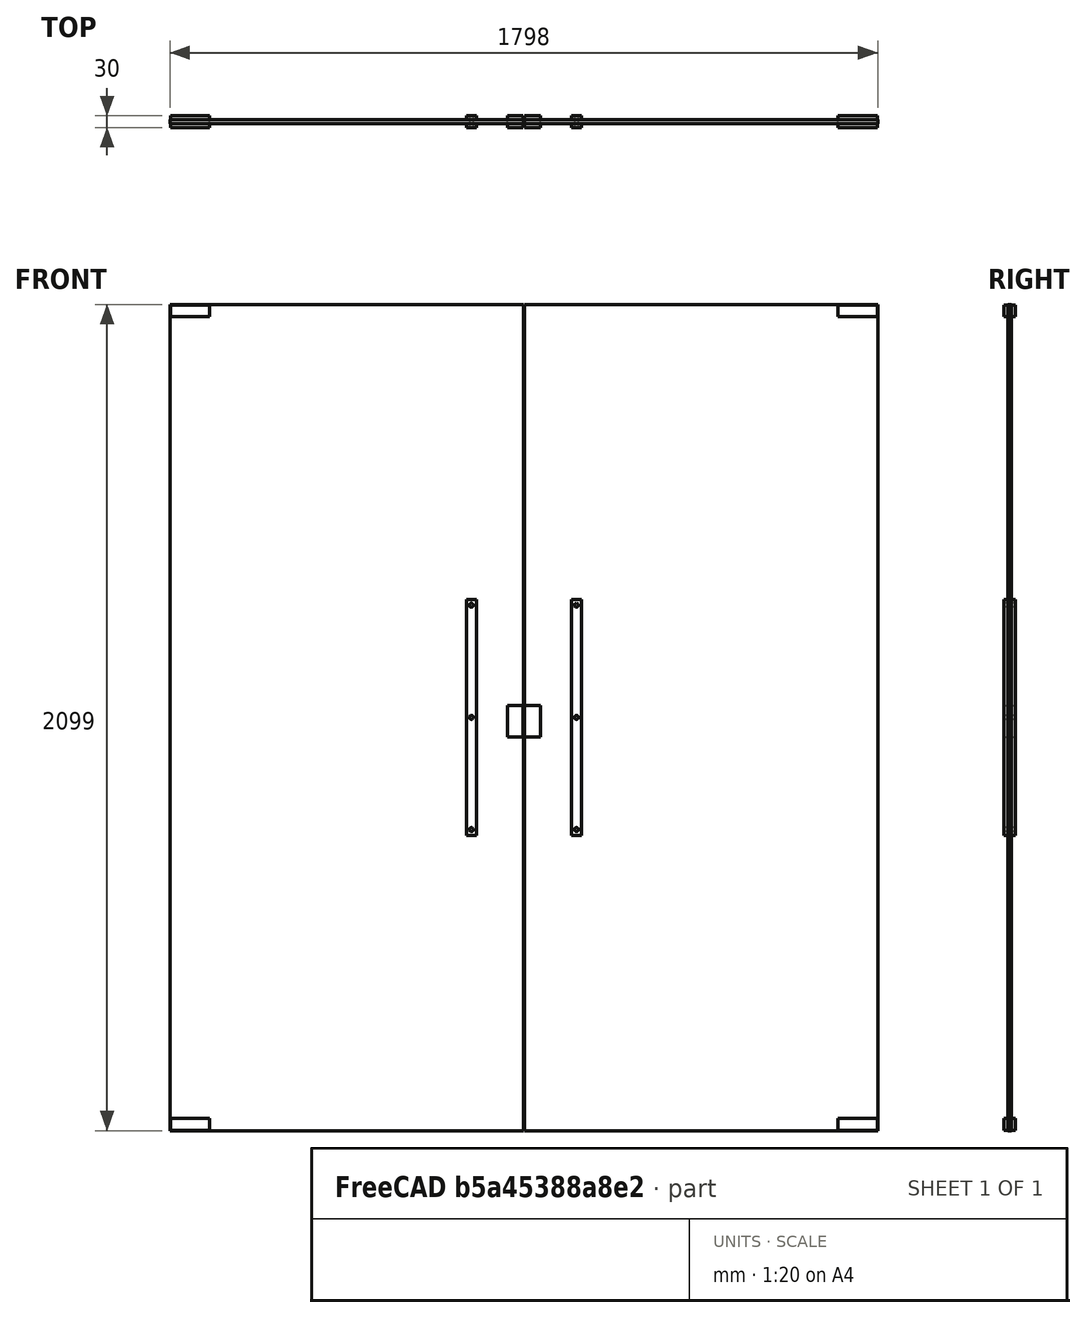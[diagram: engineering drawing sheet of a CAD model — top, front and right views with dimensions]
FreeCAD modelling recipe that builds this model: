
FCSTD DOCUMENT  (FreeCAD 0.16R6704 (Git))
Label: Double glass doors with handles
License: CreativeCommons Attribution
LicenseURL: http://creativecommons.org/licenses/by/4.0/
objects: Sketcher::SketchObject×3, Part::FeaturePython×1, App::DocumentObjectGroup×1
note: 4 computed .brp shape members not serialized (recipe doc carries the construction recipe); baked Part::Feature solids carry a one-line shape summary decoded from their .brp

FEATURE [Sketcher::SketchObject] Sketch124
  Placement = pos=(0,0,0) rot=(1,0,0;1.5708rad)
  sketch-geometry (59):
    g0: LineSegment StartX=0 StartY=0 StartZ=0 EndX=1800 EndY=0 EndZ=0
    g1: LineSegment StartX=1800 StartY=0 StartZ=0 EndX=1800 EndY=2100 EndZ=0
    g2: LineSegment StartX=1800 StartY=2100 StartZ=0 EndX=0 EndY=2100 EndZ=0
    g3: LineSegment StartX=0 StartY=2100 StartZ=0 EndX=0 EndY=0 EndZ=0
    g4: LineSegment StartX=1 StartY=0 StartZ=0 EndX=899 EndY=0 EndZ=0
    g5: LineSegment StartX=899 StartY=0 StartZ=0 EndX=899 EndY=2099 EndZ=0
    g6: LineSegment StartX=899 StartY=2099 StartZ=0 EndX=1 EndY=2099 EndZ=0
    g7: LineSegment StartX=1 StartY=2099 StartZ=0 EndX=1 EndY=0 EndZ=0
    g8: LineSegment StartX=2 StartY=2098 StartZ=0 EndX=102 EndY=2098 EndZ=0
    g9: LineSegment StartX=102 StartY=2098 StartZ=0 EndX=102 EndY=2068 EndZ=0
    g10: LineSegment StartX=102 StartY=2068 StartZ=0 EndX=2 EndY=2068 EndZ=0
    g11: LineSegment StartX=2 StartY=2068 StartZ=0 EndX=2 EndY=2098 EndZ=0
    g12: LineSegment StartX=2 StartY=1 StartZ=0 EndX=102 EndY=1 EndZ=0
    g13: LineSegment StartX=102 StartY=1 StartZ=0 EndX=102 EndY=31 EndZ=0
    g14: LineSegment StartX=102 StartY=31 StartZ=0 EndX=2 EndY=31 EndZ=0
    g15: LineSegment StartX=2 StartY=31 StartZ=0 EndX=2 EndY=1 EndZ=0
    g16: LineSegment StartX=858 StartY=1080 StartZ=0 EndX=898 EndY=1080 EndZ=0
    g17: LineSegment StartX=898 StartY=1080 StartZ=0 EndX=898 EndY=1000 EndZ=0
    g18: LineSegment StartX=898 StartY=1000 StartZ=0 EndX=858 EndY=1000 EndZ=0
    g19: LineSegment StartX=858 StartY=1000 StartZ=0 EndX=858 EndY=1080 EndZ=0
    g20: LineSegment StartX=754 StartY=1350 StartZ=0 EndX=779 EndY=1350 EndZ=0
    g21: LineSegment StartX=779 StartY=1350 StartZ=0 EndX=779 EndY=750 EndZ=0
    g22: LineSegment StartX=779 StartY=750 StartZ=0 EndX=754 EndY=750 EndZ=0
    g23: LineSegment StartX=754 StartY=750 StartZ=0 EndX=754 EndY=1350 EndZ=0
    g24: LineSegment [constr] StartX=766.5 StartY=1477.64 StartZ=0 EndX=766.5 EndY=711 EndZ=0
    g25: Circle CenterX=766.5 CenterY=1335 CenterZ=0 NormalX=0 NormalY=0 NormalZ=1 Radius=5
    g26: Circle CenterX=766.5 CenterY=1050 CenterZ=0 NormalX=0 NormalY=0 NormalZ=1 Radius=5
    g27: Circle CenterX=766.5 CenterY=765 CenterZ=0 NormalX=0 NormalY=0 NormalZ=1 Radius=5
    g28: LineSegment [constr] StartX=712 StartY=1050 StartZ=0 EndX=790 EndY=1050 EndZ=0
    g29: LineSegment [constr] StartX=900 StartY=2725.39 StartZ=0 EndX=900 EndY=-391.222 EndZ=0
    g30: LineSegment StartX=1799 StartY=1e-12 StartZ=0 EndX=901 EndY=1e-12 EndZ=0
    g31: LineSegment StartX=901 StartY=1e-12 StartZ=0 EndX=901 EndY=2099 EndZ=0
    g32: LineSegment StartX=901 StartY=2099 StartZ=0 EndX=1799 EndY=2099 EndZ=0
    g33: LineSegment StartX=1799 StartY=2099 StartZ=0 EndX=1799 EndY=1e-12 EndZ=0
    g34: LineSegment StartX=1798 StartY=2098 StartZ=0 EndX=1698 EndY=2098 EndZ=0
    g35: LineSegment StartX=1698 StartY=2098 StartZ=0 EndX=1698 EndY=2068 EndZ=0
    g36: LineSegment StartX=1698 StartY=2068 StartZ=0 EndX=1798 EndY=2068 EndZ=0
    g37: LineSegment StartX=1798 StartY=2068 StartZ=0 EndX=1798 EndY=2098 EndZ=0
    g38: LineSegment StartX=1798 StartY=1 StartZ=0 EndX=1698 EndY=1 EndZ=0
    g39: LineSegment StartX=1698 StartY=1 StartZ=0 EndX=1698 EndY=31 EndZ=0
    g40: LineSegment StartX=1698 StartY=31 StartZ=0 EndX=1798 EndY=31 EndZ=0
    g41: LineSegment StartX=1798 StartY=31 StartZ=0 EndX=1798 EndY=1 EndZ=0
    g42: LineSegment StartX=942 StartY=1080 StartZ=0 EndX=902 EndY=1080 EndZ=0
    g43: LineSegment StartX=902 StartY=1080 StartZ=0 EndX=902 EndY=1000 EndZ=0
    g44: LineSegment StartX=902 StartY=1000 StartZ=0 EndX=942 EndY=1000 EndZ=0
    g45: LineSegment StartX=942 StartY=1000 StartZ=0 EndX=942 EndY=1080 EndZ=0
    g46: LineSegment StartX=1046 StartY=1350 StartZ=0 EndX=1021 EndY=1350 EndZ=0
    g47: LineSegment StartX=1021 StartY=1350 StartZ=0 EndX=1021 EndY=750 EndZ=0
    g48: LineSegment StartX=1021 StartY=750 StartZ=0 EndX=1046 EndY=750 EndZ=0
    g49: LineSegment StartX=1046 StartY=750 StartZ=0 EndX=1046 EndY=1350 EndZ=0
    g50: LineSegment [constr] StartX=1033.5 StartY=1477.64 StartZ=0 EndX=1033.5 EndY=711 EndZ=0
    g51: Circle CenterX=1033.5 CenterY=1335 CenterZ=0 NormalX=0 NormalY=0 NormalZ=1 Radius=5
    g52: Circle CenterX=1033.5 CenterY=1050 CenterZ=0 NormalX=0 NormalY=0 NormalZ=1 Radius=5
    g53: Circle CenterX=1033.5 CenterY=765 CenterZ=0 NormalX=0 NormalY=0 NormalZ=1 Radius=5
    g54: LineSegment [constr] StartX=1088 StartY=1050 StartZ=0 EndX=1010 EndY=1050 EndZ=0
    g55: LineSegment StartX=-1 StartY=2101 StartZ=0 EndX=1801 EndY=2101 EndZ=0
    g56: LineSegment StartX=1801 StartY=2101 StartZ=0 EndX=1801 EndY=0 EndZ=0
    g57: LineSegment StartX=1801 StartY=0 StartZ=0 EndX=-1 EndY=0 EndZ=0
    g58: LineSegment StartX=-1 StartY=0 StartZ=0 EndX=-1 EndY=2101 EndZ=0
  constraints (150):
    c: Coincident(g0,g1)
    c: Coincident(g1,g2)
    c: Coincident(g2,g3)
    c: Coincident(g3,g0)
    c: Horizontal(g0)
    c: Horizontal(g2)
    c: Vertical(g1)
    c: Vertical(g3)
    c: Coincident(g4,g5)
    c: Coincident(g5,g6)
    c: Coincident(g6,g7)
    c: Coincident(g7,g4)
    c: Horizontal(g4)
    c: Horizontal(g6)
    c: Vertical(g5)
    c: Vertical(g7)
    c: DistanceY(g1) = 2100  'Altura vão'
    c: DistanceX(g0) = 1800  'Largura vão'
    c: DistanceY(g6,g2) = 1
    c: DistanceX(g2,g6) = 1
    c: DistanceY(g0,g4) = 0
    c: Coincident(g0,g-1)
    c: Coincident(g8,g9)
    c: Coincident(g9,g10)
    c: Coincident(g10,g11)
    c: Coincident(g11,g8)
    c: Horizontal(g8)
    c: Horizontal(g10)
    c: Vertical(g9)
    c: Vertical(g11)
    c: Coincident(g12,g13)
    c: Coincident(g13,g14)
    c: Coincident(g14,g15)
    c: Coincident(g15,g12)
    c: Horizontal(g12)
    c: Horizontal(g14)
    c: Vertical(g13)
    c: Vertical(g15)
    c: Coincident(g16,g17)
    c: Coincident(g17,g18)
    c: Coincident(g18,g19)
    c: Coincident(g19,g16)
    c: Horizontal(g16)
    c: Horizontal(g18)
    c: Vertical(g17)
    c: Vertical(g19)
    c: DistanceY(g8,g6) = 1
    c: DistanceX(g6,g8) = 1
    c: DistanceY(g9,g8) = 30  'Altura apoio'
    c: DistanceX(g10,g9) = 100  'Largura apoio'
    c: Equal(g9,g13)
    c: Equal(g14,g8)
    c: DistanceX(g4,g12) = 1
    c: DistanceY(g4,g12) = 1
    c: DistanceX(g17,g4) = 1
    c: DistanceY(g18,g16) = 80  'Altura da tranca'
    c: DistanceX(g16,g16) = 40  'Largura da tranca'
    c: DistanceY(g4,g18) = 1000  'Altura da tranca ao chão'
    c: Coincident(g20,g21)
    c: Coincident(g21,g22)
    c: Coincident(g22,g23)
    c: Coincident(g23,g20)
    c: Horizontal(g20)
    c: Horizontal(g22)
    c: Vertical(g21)
    c: Vertical(g23)
    c: DistanceX(g20,g20) = 25  'Largura puxador'
    c: DistanceY(g21,g20) = 600  'altura do puxador'
    c: Vertical(g24)  'Constraint69'
    c: Symmetric(g20,g20,g24)
    c: PointOnObject(g25,g24)  'Constraint72'
    c: PointOnObject(g26,g24)
    c: PointOnObject(g27,g24)
    c: Radius(g27) = 5  'Apoio puxador'
    c: Equal(g27,g26)  'Constraint83'
    c: Equal(g27,g25)  'Constraint82'
    c: DistanceY(g25,g20) = 15
    c: DistanceY(g21,g27) = 15
    c: Horizontal(g28)
    c: PointOnObject(g26,g28)
    c: Symmetric(g22,g20,g28)
    c: DistanceY(g4,g21) = 750  'Distância do puxador ao solo'
    c: DistanceX(g21,g4) = 120  'Distância do puxador'
    c: Vertical(g29)
    c: Symmetric(g2,g1,g29)
    c: Coincident(g30,g31)
    c: Coincident(g31,g32)
    c: Coincident(g32,g33)
    c: Coincident(g33,g30)
    c: Horizontal(g30)
    c: Horizontal(g32)
    c: Vertical(g31)
    c: Vertical(g33)
    c: Coincident(g34,g35)
    c: Coincident(g35,g36)
    c: Coincident(g36,g37)
    c: Coincident(g37,g34)
    c: Horizontal(g34)
    c: Horizontal(g36)
    c: Vertical(g35)
    c: Vertical(g37)
    c: Coincident(g38,g39)
    c: Coincident(g39,g40)
    c: Coincident(g40,g41)
    c: Coincident(g41,g38)
    c: Horizontal(g38)
    c: Horizontal(g40)
    c: Vertical(g39)
    c: Vertical(g41)
    c: Coincident(g42,g43)
    c: Coincident(g43,g44)
    c: Coincident(g44,g45)
    c: Coincident(g45,g42)
    c: Horizontal(g42)
    c: Horizontal(g44)
    c: Vertical(g43)
    c: Vertical(g45)
    c: Equal(g35,g39)
    c: Equal(g40,g34)
    c: Coincident(g46,g47)
    c: Coincident(g47,g48)
    c: Coincident(g48,g49)
    c: Coincident(g49,g46)
    c: Horizontal(g46)
    c: Horizontal(g48)
    c: Vertical(g47)
    c: Vertical(g49)
    c: Vertical(g50)  'Constraint69'
    c: Symmetric(g46,g46,g50)
    c: PointOnObject(g51,g50)  'Constraint72'
    c: PointOnObject(g52,g50)
    c: PointOnObject(g53,g50)
    c: Radius(g53) = 5  'Apoio puxador'
    c: Equal(g53,g52)  'Constraint83'
    c: Equal(g53,g51)  'Constraint82'
    c: Horizontal(g54)
    c: PointOnObject(g52,g54)
    c: Symmetric(g48,g46,g54)
    c: Coincident(g55,g56)
    c: Coincident(g56,g57)
    c: Coincident(g57,g58)
    c: Coincident(g58,g55)
    c: Horizontal(g55)
    c: Horizontal(g57)
    c: Vertical(g56)
    c: Vertical(g58)
    c: DistanceX(g55,g2) = 1
    c: DistanceY(g2,g55) = 1
    c: DistanceX(g1,g55) = 1
    c: DistanceY(g57,g-1) = 0
FEATURE [Part::FeaturePython] Window091  label="Double glass doors with handles 001"  # WARN: FeaturePython — macro-defined, semantics opaque (R4)
  Base = -> Sketch124
  Height = 2100
  HoleDepth = 0
  MoveWithHost = true
  Normal = (0,1,0)
  Preset = 6
  Role = 1
  Width = 900
  WindowParts = PORTA 1 | Glass panel | Wire1 | 10.0 | 10.0 | APOIO SUPERIOR PORTA 1 | Frame | Wire2 | 30.0 | 0.0 | APOIO INFERIOR PORTA 1 | Frame | Wire3 | 30.0 | 0.0 | TRANCA 1 | Frame | Wire4 | 30.0 | 0.0 | PUXADOR 1a | Frame | Wire5 | 10.0 | 0.0 | PUXADOR 2 | Frame | Wire13 | 10.0 | 0.0 | APOIO SUPERIRO PUXADOR 1 | Frame | Wire6 | 30.0 | 0.0 | APOIO CENTRAL PUXADOR 1 | Frame | Wire7 | 30.0 | 0.0 | APOIO INFERIRO PUXADOR 1 | Frame | Wire8 | 30.0 | 0.0 | PORTA 2 | Glass panel | Wire9 | 10.0 | 10.0 | APOIOS SUPERIRO PORTA 2 | Frame | Wire10 | 30.0 | 0.0 | APOIO INFERIRO PORTA 2 | Frame | Wire11 | 30.0 | 0.0 | TRANCA 2 | Frame | Wire12 | 30.0 | 0.0 | APOIO SUPERIOR PUXADOR 2 | Frame | Wire14 | 30.0 | 0.0 | APOIO CENTRAL PUXADOR 2 | Frame | Wire15 | 30.0 | 0.0 | APOIO INFERIOR PUXADOR 2 | Frame | Wire16 | 30.0 | 0.0 | PUXADOR 2b | Frame | Wire13 | 10.0 | 20.0 | PUXADOR 1B | Frame | Wire5 | 10.0 | 20.0
FEATURE [Sketcher::SketchObject] Sketch126  label="Opening indication"
  ExternalGeometry = -> [Window091]
  Placement = pos=(0,10,0) rot=(1,0,0;1.5708rad)
  Support = -> Window091 [Face5]
  sketch-geometry (6):
    g0: LineSegment [constr] StartX=-578.323 StartY=1041.81 StartZ=0 EndX=1784.68 EndY=1041.81 EndZ=0
    g1: LineSegment [constr] StartX=60 StartY=2218.7 StartZ=0 EndX=60 EndY=-135.607 EndZ=0
    g2: LineSegment StartX=1 StartY=1041.81 StartZ=0 EndX=60 EndY=2099 EndZ=0
    g3: LineSegment StartX=60 StartY=2099 StartZ=0 EndX=899 EndY=1041.81 EndZ=0
    g4: LineSegment StartX=899 StartY=1041.81 StartZ=0 EndX=60 EndY=0 EndZ=0
    g5: LineSegment StartX=60 StartY=0 StartZ=0 EndX=1 EndY=1041.81 EndZ=0
  constraints (16):
    c: Horizontal(g0)
    c: DistanceY(g-1,g0) = 1041.81  'Altura tranca'
    c: Vertical(g1)
    c: PointOnObject(g2,g-4)
    c: PointOnObject(g2,g-3)
    c: Coincident(g2,g3)
    c: PointOnObject(g3,g-5)
    c: Coincident(g3,g4)
    c: PointOnObject(g4,g-6)
    c: Coincident(g4,g5)
    c: Coincident(g5,g2)
    c: PointOnObject(g2,g0)
    c: PointOnObject(g2,g1)
    c: PointOnObject(g3,g0)
    c: PointOnObject(g4,g1)
    c: DistanceX(g-1,g1) = 60  'Eixo porta'
FEATURE [Sketcher::SketchObject] Sketch127  label="Opening indication  "
  ExternalGeometry = -> [Window091]
  Placement = pos=(0,10,0) rot=(1,0,0;1.5708rad)
  Support = -> Window091 [Face50]
  sketch-geometry (6):
    g0: LineSegment [constr] StartX=-496.649 StartY=1041.19 StartZ=0 EndX=2033.7 EndY=1041.19 EndZ=0
    g1: LineSegment StartX=1739 StartY=2099 StartZ=0 EndX=899 EndY=1041.19 EndZ=0
    g2: LineSegment StartX=899 StartY=1041.19 StartZ=0 EndX=1739 EndY=1e-12 EndZ=0
    g3: LineSegment StartX=1739 StartY=1e-12 StartZ=0 EndX=1799 EndY=1041.19 EndZ=0
    g4: LineSegment StartX=1799 StartY=1041.19 StartZ=0 EndX=1739 EndY=2099 EndZ=0
    g5: LineSegment [constr] StartX=1739 StartY=2207.43 StartZ=0 EndX=1739 EndY=-73.7721 EndZ=0
  constraints (16):
    c: Horizontal(g0)
    c: DistanceY(g-1,g0) = 1041.19  'Altura da tranca'
    c: PointOnObject(g1,g-3)
    c: PointOnObject(g1,g-4)
    c: Coincident(g1,g2)
    c: PointOnObject(g2,g-6)
    c: Coincident(g2,g3)
    c: PointOnObject(g3,g-5)
    c: Coincident(g3,g4)
    c: Coincident(g1,g4)
    c: Vertical(g5)
    c: DistanceX(g5,g-6) = 60  'Eixo porta'
    c: PointOnObject(g3,g0)
    c: PointOnObject(g2,g5)
    c: PointOnObject(g1,g0)
    c: PointOnObject(g1,g5)
FEATURE [App::DocumentObjectGroup] Grupo098  label="Double glass doors with handles "
  Group = -> [Window091,Sketch126,Sketch127]
